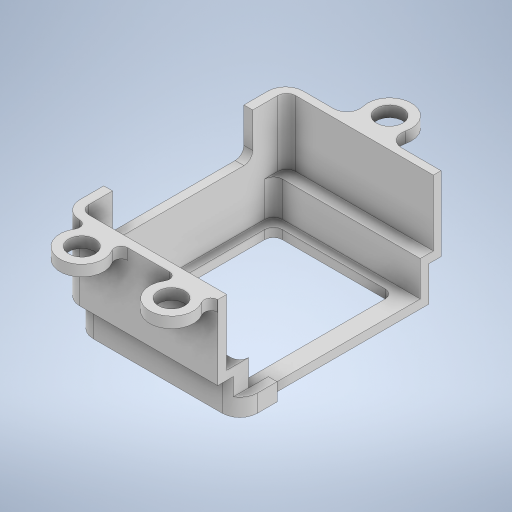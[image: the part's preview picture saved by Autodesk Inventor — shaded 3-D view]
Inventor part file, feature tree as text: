
AUTODESK INVENTOR PART (.ipt)
format: ipt  version: 2023 (Build 270158000, 158)  size: 483,328 bytes
history: native  units: in
note: dims shown in document units (in); Inventor stores cm internally (conversion verified against a paired STEP export)
features: extrude x8, sketch x4, projected_geometry x2, plane x1
ambient origin geometry x8: Origin, YZ Plane, XZ Plane, XY Plane, X Axis, Y Axis, Z Axis, Center Point
bodies: Body1 (feature_tree)
feature tree (15):
  extrude  "Extrusion3"  Depth=0.0787in
  plane  "Work Plane1"
  extrude  "Extrusion4"  Depth=0.315in TaperAngle=0.0deg
  extrude  "Extrusion7"  Depth=0.0787in TaperAngle=0.0deg
  extrude  "Extrusion8"  Depth=0.3937in
  extrude  "Extrusion10"  Depth=0.2362in
  extrude  "Extrusion11"  Depth=0.1181in
  extrude  "Extrusion12"  Depth=0.1181in
  extrude  "Extrusion13"  Depth=0.3937in
  sketch  "Sketch5"  dims[d8=0.0787in d9=0.0787in]
  sketch  "Sketch6"  dims[d10=0.0787in d11=0.0in d12=0.315in d13=0.0in]
  projected_geometry  "Projected Loop3"
  sketch  "Sketch7"  dims[d14=0.315in d28=0.0787in d29=0.0in]
  sketch  "Sketch8"  dims[d30=0.5906in d31=0.0in d34=0.3937in d35=0.2362in d38=0.1181in d39=0.1181in d40=0.3937in d41=0.2362in d42=0.1181in d43=0.1181in d44=0.3937in d45=0.2362in d47=0.1181in d49=0.8071in d50=0.0984in d51=0.0in d52=0.1575in d53=1.4646in d54=1.0827in d55=0.1575in d56=0.0787in d57=0.0787in d58=0.0in d59=0.0787in d61=1.2598in d64=0.2362in d65=0.0in d66=0.0787in d67=0.0787in d68=0.1772in d69=0.1575in d70=0.2362in d71=0.0in d79=1.6929in d80=1.2402in d81=0.1575in d83=0.187in d85=0.0394in d87=0.0394in d88=0.1181in d89=0.7382in d90=0.2165in d91=0.3937in]
  projected_geometry  "Projected Loop4"
